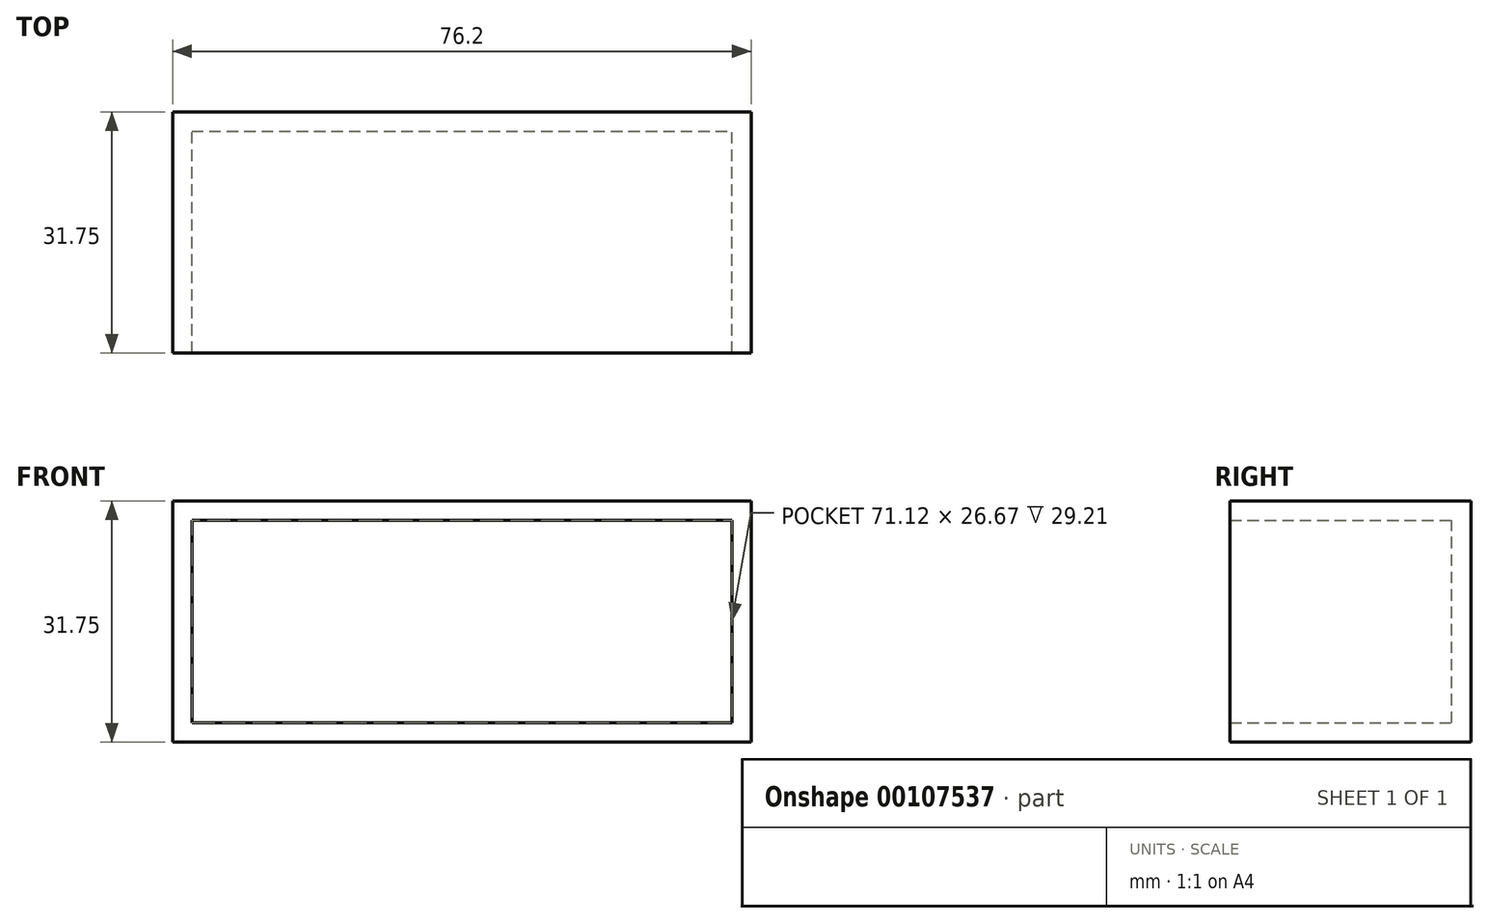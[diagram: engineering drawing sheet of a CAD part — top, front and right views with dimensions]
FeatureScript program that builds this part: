
annotation { "Feature Type Name" : "Feature", "Feature Type Description" : "" }
export const myFeature = defineFeature(function(context is Context, id is Id, definition is map)
    precondition{}
    {
        {
            var Q0;
            Q0=qCreatedBy(makeId("Front.planeOp"),FACE);
            var sketch = newSketch(context, id + "F0", { "sketchPlane" : qUnion([Q0])});
            skLineSegment(sketch, "E0.bottom", {"start": v(-25.67, 11.28) * mm, "end": v(50.53, 11.28) * mm});
            skLineSegment(sketch, "E0.top", {"start": v(-25.67, 43.03) * mm, "end": v(50.53, 43.03) * mm});
            skLineSegment(sketch, "E0.left", {"start": v(-25.67, 11.28) * mm, "end": v(-25.67, 43.03) * mm});
            skLineSegment(sketch, "E0.right", {"start": v(50.53, 11.28) * mm, "end": v(50.53, 43.03) * mm});
            skArc(sketch, "E1", {"start": v(-25.67, 43.03) * mm, "mid": v(-41.54, 27.15) * mm, "end": v(-25.67, 11.28) * mm});
            skSolve(sketch);
        }
        {
            var Q0;
            Q0=makeQuery(id+"F0.imprint","IMPRINT",FACE,{"disambiguationData":[TD([[makeQuery(id+"F0.imprint","IMPRINT",EDGE,{"derivedFrom":sQuery(id+"F0.wireOp",EDGE,"E0.bottom")}),1.0]])]});
            extrude(context, id + "F1", {"entities" : qUnion([Q0]), "depth" : 31.75 * mm});
        }
        {
            var Q0;
            Q0=makeQuery(id+"F1.opExtrude","CAP_FACE",FACE,{"disambiguationData":[OSD([sQuery(id+"F0.wireOp",EDGE,"E0.bottom"),sQuery(id+"F0.wireOp",EDGE,"E0.top"),sQuery(id+"F0.wireOp",EDGE,"E0.left"),sQuery(id+"F0.wireOp",EDGE,"E0.right")])],"isStart":false});
            shell(context, id + "F2", {"entities" : qUnion([Q0]), "thickness" : 2.54 * mm});
        }
    });
